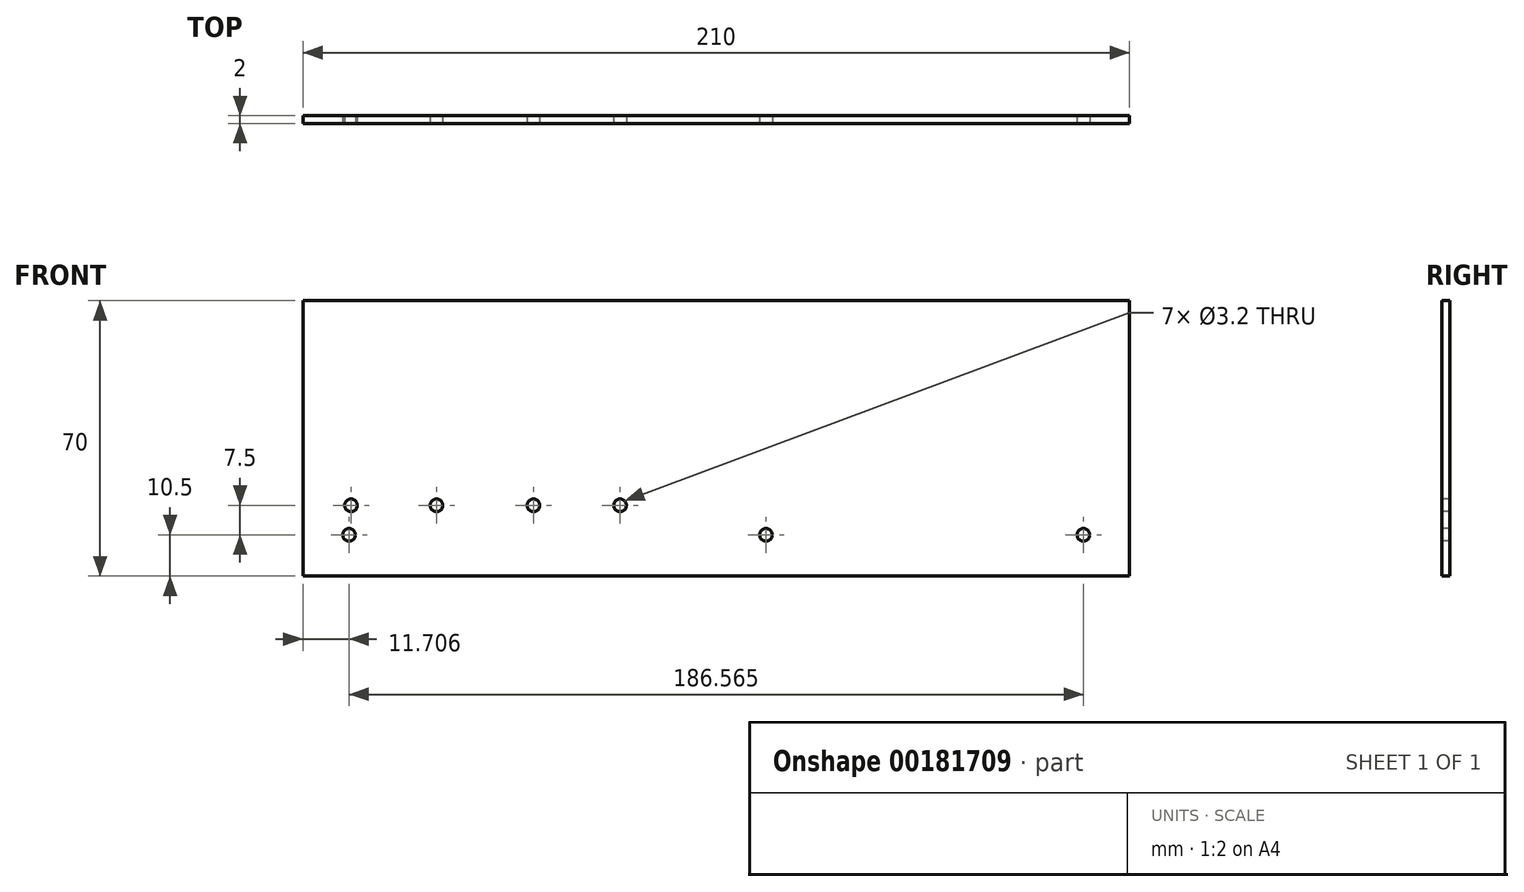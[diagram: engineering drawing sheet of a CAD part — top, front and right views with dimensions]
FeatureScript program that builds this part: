
annotation { "Feature Type Name" : "Feature", "Feature Type Description" : "" }
export const myFeature = defineFeature(function(context is Context, id is Id, definition is map)
    precondition{}
    {
        {
            var Q0;
            Q0=qCreatedBy(makeId("Front.planeOp"),FACE);
            var sketch = newSketch(context, id + "F0", { "sketchPlane" : qUnion([Q0])});
            skLineSegment(sketch, "E0.bottom", {"start": v(0, 0) * mm, "end": v(210, 0) * mm});
            skLineSegment(sketch, "E0.top", {"start": v(0, 70) * mm, "end": v(210, 70) * mm});
            skLineSegment(sketch, "E0.left", {"start": v(0, 0) * mm, "end": v(0, 70) * mm});
            skLineSegment(sketch, "E0.right", {"start": v(210, 0) * mm, "end": v(210, 70) * mm});
            skSolve(sketch);
        }
        {
            var Q0;
            Q0=makeQuery(id+"F0.imprint","IMPRINT",FACE,{"disambiguationData":[TD([[makeQuery(id+"F0.imprint","IMPRINT",EDGE,{"derivedFrom":sQuery(id+"F0.wireOp",EDGE,"E0.bottom")}),1.0]])]});
            extrude(context, id + "F1", {"entities" : qUnion([Q0]), "depth" : 2 * mm});
        }
        {
            var Q0;
            Q0=makeQuery(id+"F1.opExtrude","CAP_FACE",FACE,{"disambiguationData":[OSD([sQuery(id+"F0.wireOp",EDGE,"E0.bottom"),sQuery(id+"F0.wireOp",EDGE,"E0.top"),sQuery(id+"F0.wireOp",EDGE,"E0.left"),sQuery(id+"F0.wireOp",EDGE,"E0.right")])],"isStart":false});
            var sketch = newSketch(context, id + "F2", { "sketchPlane" : qUnion([Q0])});
            skPoint(sketch, "E1", {"position": v(11.7, 10.5) * mm});
            skPoint(sketch, "E2", {"position": v(117.62, 10.5) * mm});
            skPoint(sketch, "E3", {"position": v(198.27, 10.5) * mm});
            skPoint(sketch, "E4", {"position": v(12.2, 18) * mm});
            skPoint(sketch, "E5", {"position": v(33.91, 18) * mm});
            skPoint(sketch, "E6", {"position": v(58.55, 18) * mm});
            skPoint(sketch, "E7", {"position": v(80.56, 18) * mm});
            skSolve(sketch);
        }
        {
            var Q0;
            Q0=sQuery(id+"F2.wireOp",VERTEX,"E4");
            var Q1;
            Q1=sQuery(id+"F2.wireOp",VERTEX,"E1");
            var Q2;
            Q2=sQuery(id+"F2.wireOp",VERTEX,"E5");
            var Q3;
            Q3=sQuery(id+"F2.wireOp",VERTEX,"E6");
            var Q4;
            Q4=sQuery(id+"F2.wireOp",VERTEX,"E7");
            var Q5;
            Q5=sQuery(id+"F2.wireOp",VERTEX,"E2");
            var Q6;
            Q6=sQuery(id+"F2.wireOp",VERTEX,"E3");
            var Q7;
            Q7=makeQuery(id+"F1.opExtrude","SWEPT_BODY",BODY,{"disambiguationData":[OSD([sQuery(id+"F0.wireOp",EDGE,"E0.bottom"),sQuery(id+"F0.wireOp",EDGE,"E0.top"),sQuery(id+"F0.wireOp",EDGE,"E0.left"),sQuery(id+"F0.wireOp",EDGE,"E0.right")])]});
            hole(context, id + "F3", {"style" : HoleStyle.SIMPLE, "endStyle" : HoleEndStyle.THROUGH, "holeDiameter" : 3.2 * mm, "locations" : qUnion([Q0, Q1, Q2, Q3, Q4, Q5, Q6]), "scope" : qUnion([Q7]), "isTappedThrough" : true});
        }
    });
